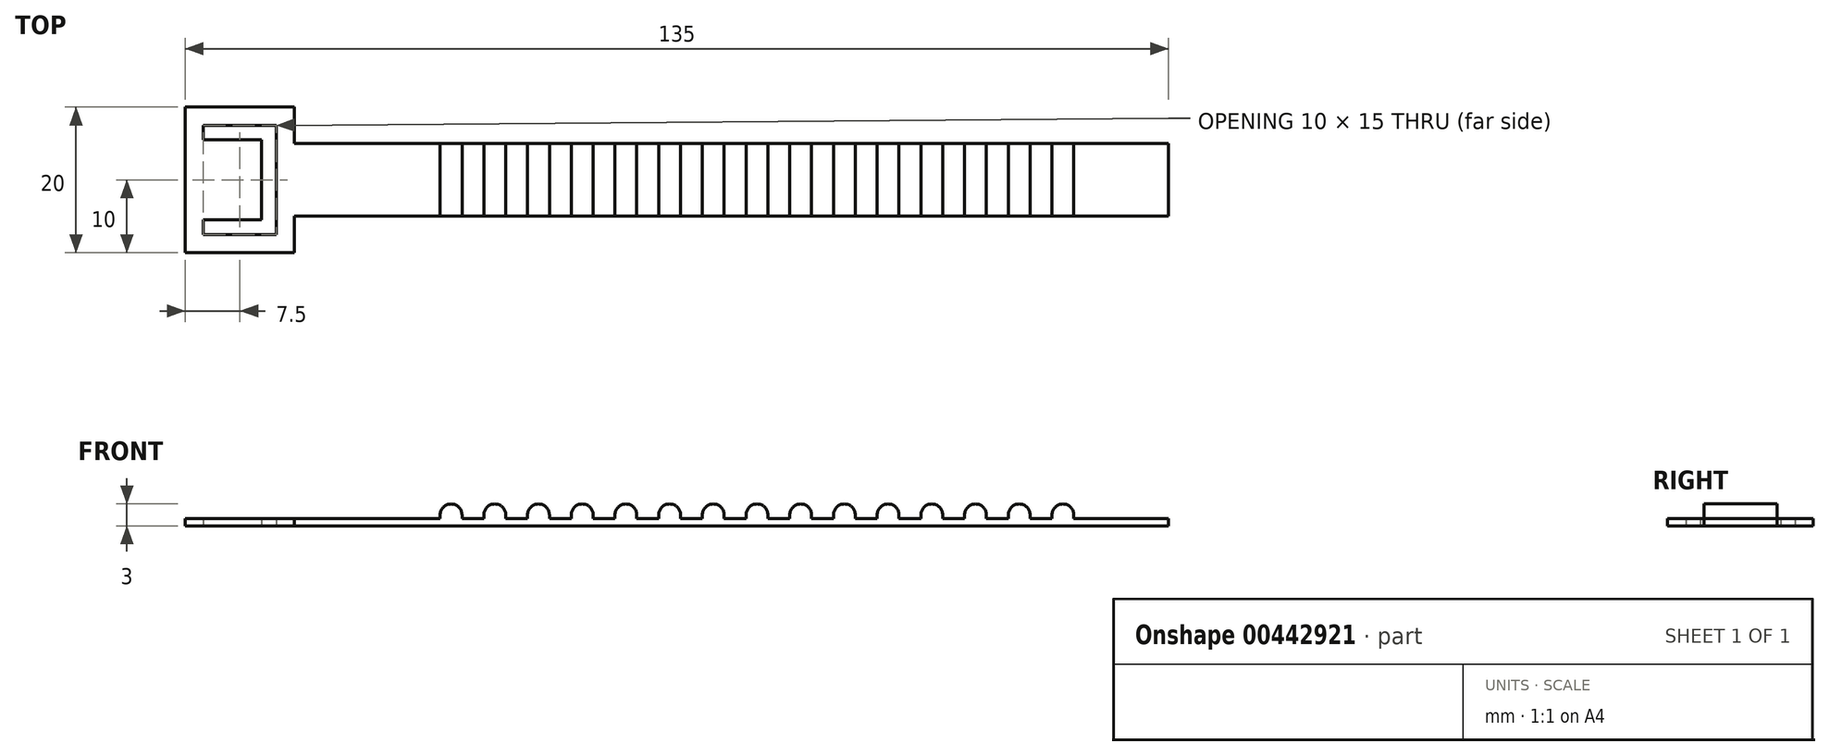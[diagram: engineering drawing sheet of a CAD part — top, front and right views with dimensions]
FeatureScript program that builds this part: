
annotation { "Feature Type Name" : "Feature", "Feature Type Description" : "" }
export const myFeature = defineFeature(function(context is Context, id is Id, definition is map)
    precondition{}
    {
        {
            var Q0;
            Q0=qCreatedBy(makeId("Top.planeOp"),FACE);
            var sketch = newSketch(context, id + "F0", { "sketchPlane" : qUnion([Q0])});
            skLineSegment(sketch, "E0.bottom", {"start": v(-60, 5) * mm, "end": v(60, 5) * mm});
            skLineSegment(sketch, "E0.top", {"start": v(-60, -5) * mm, "end": v(60, -5) * mm});
            skLineSegment(sketch, "E0.left", {"start": v(-60, 5) * mm, "end": v(-60, -5) * mm});
            skLineSegment(sketch, "E0.right", {"start": v(60, 5) * mm, "end": v(60, -5) * mm});
            skPoint(sketch, "E0.middle", {"position": v(0, 0) * mm});
            skLineSegment(sketch, "E1.bottom", {"start": v(-75, 10) * mm, "end": v(-60, 10) * mm});
            skLineSegment(sketch, "E1.top", {"start": v(-75, -10) * mm, "end": v(-60, -10) * mm});
            skLineSegment(sketch, "E1.left", {"start": v(-75, 10) * mm, "end": v(-75, -10) * mm});
            skLineSegment(sketch, "E1.right", {"start": v(-60, 10) * mm, "end": v(-60, -10) * mm});
            skPoint(sketch, "E1.middle", {"position": v(-67.5, 0) * mm});
            skLineSegment(sketch, "E2", {"start": v(-72.5, 7.5) * mm, "end": v(-62.5, 7.5) * mm});
            skLineSegment(sketch, "E3", {"start": v(-62.5, 7.5) * mm, "end": v(-62.5, -7.5) * mm});
            skLineSegment(sketch, "E4", {"start": v(-62.5, -7.5) * mm, "end": v(-72.5, -7.5) * mm});
            skLineSegment(sketch, "E5", {"start": v(-72.5, -7.5) * mm, "end": v(-72.5, -5.5) * mm});
            skLineSegment(sketch, "E6", {"start": v(-72.5, -5.5) * mm, "end": v(-64.5, -5.5) * mm});
            skLineSegment(sketch, "E7", {"start": v(-64.5, -5.5) * mm, "end": v(-64.5, 5.5) * mm});
            skLineSegment(sketch, "E8", {"start": v(-64.5, 5.5) * mm, "end": v(-72.5, 5.5) * mm});
            skLineSegment(sketch, "E9", {"start": v(-72.5, 5.5) * mm, "end": v(-72.5, 7.5) * mm});
            skSolve(sketch);
        }
        {
            var Q0;
            Q0 = qSketchRegion(id + "F0", true);
            extrude(context, id + "F1", {"entities" : qUnion([Q0]), "depth" : 1 * mm});
        }
        {
            var Q0;
            Q0=qCreatedBy(makeId("Top.planeOp"),FACE);
            var sketch = newSketch(context, id + "F2", { "sketchPlane" : qUnion([Q0])});
            skLineSegment(sketch, "E10.bottom", {"start": v(-37, 5) * mm, "end": v(-40, 5) * mm});
            skLineSegment(sketch, "E10.top", {"start": v(-37, -5) * mm, "end": v(-40, -5) * mm});
            skLineSegment(sketch, "E10.left", {"start": v(-37, 5) * mm, "end": v(-37, -5) * mm});
            skLineSegment(sketch, "E10.right", {"start": v(-40, 5) * mm, "end": v(-40, -5) * mm});
            skPoint(sketch, "E10.middle", {"position": v(-38.5, 0) * mm});
            skLineSegment(sketch, "E11.1.0.0", {"start": v(-34, 5) * mm, "end": v(-34, -5) * mm});
            skLineSegment(sketch, "E11.1.0.1", {"start": v(-31, 5) * mm, "end": v(-31, -5) * mm});
            skLineSegment(sketch, "E11.1.0.2", {"start": v(-31, 5) * mm, "end": v(-34, 5) * mm});
            skLineSegment(sketch, "E11.1.0.3", {"start": v(-31, -5) * mm, "end": v(-34, -5) * mm});
            skLineSegment(sketch, "E11.2.0.0", {"start": v(-28, 5) * mm, "end": v(-28, -5) * mm});
            skLineSegment(sketch, "E11.2.0.1", {"start": v(-25, 5) * mm, "end": v(-25, -5) * mm});
            skLineSegment(sketch, "E11.2.0.2", {"start": v(-25, 5) * mm, "end": v(-28, 5) * mm});
            skLineSegment(sketch, "E11.2.0.3", {"start": v(-25, -5) * mm, "end": v(-28, -5) * mm});
            skLineSegment(sketch, "E11.3.0.0", {"start": v(-22, 5) * mm, "end": v(-22, -5) * mm});
            skLineSegment(sketch, "E11.3.0.1", {"start": v(-19, 5) * mm, "end": v(-19, -5) * mm});
            skLineSegment(sketch, "E11.3.0.2", {"start": v(-19, 5) * mm, "end": v(-22, 5) * mm});
            skLineSegment(sketch, "E11.3.0.3", {"start": v(-19, -5) * mm, "end": v(-22, -5) * mm});
            skLineSegment(sketch, "E11.4.0.0", {"start": v(-16, 5) * mm, "end": v(-16, -5) * mm});
            skLineSegment(sketch, "E11.4.0.1", {"start": v(-13, 5) * mm, "end": v(-13, -5) * mm});
            skLineSegment(sketch, "E11.4.0.2", {"start": v(-13, 5) * mm, "end": v(-16, 5) * mm});
            skLineSegment(sketch, "E11.4.0.3", {"start": v(-13, -5) * mm, "end": v(-16, -5) * mm});
            skLineSegment(sketch, "E11.5.0.0", {"start": v(-10, 5) * mm, "end": v(-10, -5) * mm});
            skLineSegment(sketch, "E11.5.0.1", {"start": v(-7, 5) * mm, "end": v(-7, -5) * mm});
            skLineSegment(sketch, "E11.5.0.2", {"start": v(-7, 5) * mm, "end": v(-10, 5) * mm});
            skLineSegment(sketch, "E11.5.0.3", {"start": v(-7, -5) * mm, "end": v(-10, -5) * mm});
            skLineSegment(sketch, "E11.6.0.0", {"start": v(-4, 5) * mm, "end": v(-4, -5) * mm});
            skLineSegment(sketch, "E11.6.0.1", {"start": v(-1, 5) * mm, "end": v(-1, -5) * mm});
            skLineSegment(sketch, "E11.6.0.2", {"start": v(-1, 5) * mm, "end": v(-4, 5) * mm});
            skLineSegment(sketch, "E11.6.0.3", {"start": v(-1, -5) * mm, "end": v(-4, -5) * mm});
            skLineSegment(sketch, "E11.7.0.0", {"start": v(2, 5) * mm, "end": v(2, -5) * mm});
            skLineSegment(sketch, "E11.7.0.1", {"start": v(5, 5) * mm, "end": v(5, -5) * mm});
            skLineSegment(sketch, "E11.7.0.2", {"start": v(5, 5) * mm, "end": v(2, 5) * mm});
            skLineSegment(sketch, "E11.7.0.3", {"start": v(5, -5) * mm, "end": v(2, -5) * mm});
            skLineSegment(sketch, "E11.8.0.0", {"start": v(8, 5) * mm, "end": v(8, -5) * mm});
            skLineSegment(sketch, "E11.8.0.1", {"start": v(11, 5) * mm, "end": v(11, -5) * mm});
            skLineSegment(sketch, "E11.8.0.2", {"start": v(11, 5) * mm, "end": v(8, 5) * mm});
            skLineSegment(sketch, "E11.8.0.3", {"start": v(11, -5) * mm, "end": v(8, -5) * mm});
            skLineSegment(sketch, "E11.9.0.0", {"start": v(14, 5) * mm, "end": v(14, -5) * mm});
            skLineSegment(sketch, "E11.9.0.1", {"start": v(17, 5) * mm, "end": v(17, -5) * mm});
            skLineSegment(sketch, "E11.9.0.2", {"start": v(17, 5) * mm, "end": v(14, 5) * mm});
            skLineSegment(sketch, "E11.9.0.3", {"start": v(17, -5) * mm, "end": v(14, -5) * mm});
            skLineSegment(sketch, "E11.10.0.0", {"start": v(20, 5) * mm, "end": v(20, -5) * mm});
            skLineSegment(sketch, "E11.10.0.1", {"start": v(23, 5) * mm, "end": v(23, -5) * mm});
            skLineSegment(sketch, "E11.10.0.2", {"start": v(23, 5) * mm, "end": v(20, 5) * mm});
            skLineSegment(sketch, "E11.10.0.3", {"start": v(23, -5) * mm, "end": v(20, -5) * mm});
            skLineSegment(sketch, "E11.11.0.0", {"start": v(26, 5) * mm, "end": v(26, -5) * mm});
            skLineSegment(sketch, "E11.11.0.1", {"start": v(29, 5) * mm, "end": v(29, -5) * mm});
            skLineSegment(sketch, "E11.11.0.2", {"start": v(29, 5) * mm, "end": v(26, 5) * mm});
            skLineSegment(sketch, "E11.11.0.3", {"start": v(29, -5) * mm, "end": v(26, -5) * mm});
            skLineSegment(sketch, "E11.12.0.0", {"start": v(32, 5) * mm, "end": v(32, -5) * mm});
            skLineSegment(sketch, "E11.12.0.1", {"start": v(35, 5) * mm, "end": v(35, -5) * mm});
            skLineSegment(sketch, "E11.12.0.2", {"start": v(35, 5) * mm, "end": v(32, 5) * mm});
            skLineSegment(sketch, "E11.12.0.3", {"start": v(35, -5) * mm, "end": v(32, -5) * mm});
            skLineSegment(sketch, "E11.13.0.0", {"start": v(38, 5) * mm, "end": v(38, -5) * mm});
            skLineSegment(sketch, "E11.13.0.1", {"start": v(41, 5) * mm, "end": v(41, -5) * mm});
            skLineSegment(sketch, "E11.13.0.2", {"start": v(41, 5) * mm, "end": v(38, 5) * mm});
            skLineSegment(sketch, "E11.13.0.3", {"start": v(41, -5) * mm, "end": v(38, -5) * mm});
            skLineSegment(sketch, "E11.14.0.0", {"start": v(44, 5) * mm, "end": v(44, -5) * mm});
            skLineSegment(sketch, "E11.14.0.1", {"start": v(47, 5) * mm, "end": v(47, -5) * mm});
            skLineSegment(sketch, "E11.14.0.2", {"start": v(47, 5) * mm, "end": v(44, 5) * mm});
            skLineSegment(sketch, "E11.14.0.3", {"start": v(47, -5) * mm, "end": v(44, -5) * mm});
            skLineSegment(sketch, "E11.direction1", {"start": v(-40, -5) * mm, "end": v(-34, -5) * mm, "construction": true});
            skSolve(sketch);
        }
        {
            var Q0;
            Q0 = qSketchRegion(id + "F2", true);
            extrude(context, id + "F3", {"entities" : qUnion([Q0]), "operationType" : NewBodyOperationType.ADD, "depth" : 3 * mm});
        }
        {
            var Q0;
            Q0=makeQuery(id+"F3.opExtrude","CAP_EDGE",EDGE,{"disambiguationData":[OSD([sQuery(id+"F2.wireOp",EDGE,"E10.right")])],"isStart":false});
            fillet(context, id + "F4", {"entities" : qUnion([Q0]), "radius" : 1.5 * mm, "tangentPropagation" : true, "allowEdgeOverflow" : false});
        }
        {
            var Q0;
            Q0=makeQuery(id+"F3.opExtrude","CAP_EDGE",EDGE,{"disambiguationData":[OSD([sQuery(id+"F2.wireOp",EDGE,"E10.left")])],"isStart":false});
            fillet(context, id + "F5", {"entities" : qUnion([Q0]), "radius" : 1.5 * mm, "tangentPropagation" : true, "allowEdgeOverflow" : false});
        }
        {
            var Q0;
            Q0=makeQuery(id+"F3.opExtrude","CAP_EDGE",EDGE,{"disambiguationData":[OSD([sQuery(id+"F2.wireOp",EDGE,"E11.1.0.0")])],"isStart":false});
            var Q1;
            Q1=makeQuery(id+"F3.opExtrude","CAP_EDGE",EDGE,{"disambiguationData":[OSD([sQuery(id+"F2.wireOp",EDGE,"E11.1.0.1")])],"isStart":false});
            var Q2;
            Q2=makeQuery(id+"F3.opExtrude","CAP_EDGE",EDGE,{"disambiguationData":[OSD([sQuery(id+"F2.wireOp",EDGE,"E11.2.0.0")])],"isStart":false});
            var Q3;
            Q3=makeQuery(id+"F3.opExtrude","CAP_EDGE",EDGE,{"disambiguationData":[OSD([sQuery(id+"F2.wireOp",EDGE,"E11.2.0.1")])],"isStart":false});
            var Q4;
            Q4=makeQuery(id+"F3.opExtrude","CAP_EDGE",EDGE,{"disambiguationData":[OSD([sQuery(id+"F2.wireOp",EDGE,"E11.3.0.0")])],"isStart":false});
            var Q5;
            Q5=makeQuery(id+"F3.opExtrude","CAP_EDGE",EDGE,{"disambiguationData":[OSD([sQuery(id+"F2.wireOp",EDGE,"E11.3.0.1")])],"isStart":false});
            var Q6;
            Q6=makeQuery(id+"F3.opExtrude","CAP_EDGE",EDGE,{"disambiguationData":[OSD([sQuery(id+"F2.wireOp",EDGE,"E11.4.0.0")])],"isStart":false});
            var Q7;
            Q7=makeQuery(id+"F3.opExtrude","CAP_EDGE",EDGE,{"disambiguationData":[OSD([sQuery(id+"F2.wireOp",EDGE,"E11.4.0.1")])],"isStart":false});
            var Q8;
            Q8=makeQuery(id+"F3.opExtrude","CAP_EDGE",EDGE,{"disambiguationData":[OSD([sQuery(id+"F2.wireOp",EDGE,"E11.5.0.0")])],"isStart":false});
            var Q9;
            Q9=makeQuery(id+"F3.opExtrude","CAP_EDGE",EDGE,{"disambiguationData":[OSD([sQuery(id+"F2.wireOp",EDGE,"E11.5.0.1")])],"isStart":false});
            var Q10;
            Q10=makeQuery(id+"F3.opExtrude","CAP_EDGE",EDGE,{"disambiguationData":[OSD([sQuery(id+"F2.wireOp",EDGE,"E11.6.0.0")])],"isStart":false});
            var Q11;
            Q11=makeQuery(id+"F3.opExtrude","CAP_EDGE",EDGE,{"disambiguationData":[OSD([sQuery(id+"F2.wireOp",EDGE,"E11.6.0.1")])],"isStart":false});
            var Q12;
            Q12=makeQuery(id+"F3.opExtrude","CAP_EDGE",EDGE,{"disambiguationData":[OSD([sQuery(id+"F2.wireOp",EDGE,"E11.7.0.0")])],"isStart":false});
            var Q13;
            Q13=makeQuery(id+"F3.opExtrude","CAP_EDGE",EDGE,{"disambiguationData":[OSD([sQuery(id+"F2.wireOp",EDGE,"E11.7.0.1")])],"isStart":false});
            var Q14;
            Q14=makeQuery(id+"F3.opExtrude","CAP_EDGE",EDGE,{"disambiguationData":[OSD([sQuery(id+"F2.wireOp",EDGE,"E11.8.0.0")])],"isStart":false});
            var Q15;
            Q15=makeQuery(id+"F3.opExtrude","CAP_EDGE",EDGE,{"disambiguationData":[OSD([sQuery(id+"F2.wireOp",EDGE,"E11.8.0.1")])],"isStart":false});
            var Q16;
            Q16=makeQuery(id+"F3.opExtrude","CAP_EDGE",EDGE,{"disambiguationData":[OSD([sQuery(id+"F2.wireOp",EDGE,"E11.9.0.0")])],"isStart":false});
            var Q17;
            Q17=makeQuery(id+"F3.opExtrude","CAP_EDGE",EDGE,{"disambiguationData":[OSD([sQuery(id+"F2.wireOp",EDGE,"E11.9.0.1")])],"isStart":false});
            var Q18;
            Q18=makeQuery(id+"F3.opExtrude","CAP_EDGE",EDGE,{"disambiguationData":[OSD([sQuery(id+"F2.wireOp",EDGE,"E11.10.0.0")])],"isStart":false});
            var Q19;
            Q19=makeQuery(id+"F3.opExtrude","CAP_EDGE",EDGE,{"disambiguationData":[OSD([sQuery(id+"F2.wireOp",EDGE,"E11.10.0.1")])],"isStart":false});
            var Q20;
            Q20=makeQuery(id+"F3.opExtrude","CAP_EDGE",EDGE,{"disambiguationData":[OSD([sQuery(id+"F2.wireOp",EDGE,"E11.11.0.0")])],"isStart":false});
            var Q21;
            Q21=makeQuery(id+"F3.opExtrude","CAP_EDGE",EDGE,{"disambiguationData":[OSD([sQuery(id+"F2.wireOp",EDGE,"E11.11.0.1")])],"isStart":false});
            var Q22;
            Q22=makeQuery(id+"F3.opExtrude","CAP_EDGE",EDGE,{"disambiguationData":[OSD([sQuery(id+"F2.wireOp",EDGE,"E11.12.0.0")])],"isStart":false});
            var Q23;
            Q23=makeQuery(id+"F3.opExtrude","CAP_EDGE",EDGE,{"disambiguationData":[OSD([sQuery(id+"F2.wireOp",EDGE,"E11.12.0.1")])],"isStart":false});
            var Q24;
            Q24=makeQuery(id+"F3.opExtrude","CAP_EDGE",EDGE,{"disambiguationData":[OSD([sQuery(id+"F2.wireOp",EDGE,"E11.13.0.0")])],"isStart":false});
            var Q25;
            Q25=makeQuery(id+"F3.opExtrude","CAP_EDGE",EDGE,{"disambiguationData":[OSD([sQuery(id+"F2.wireOp",EDGE,"E11.13.0.1")])],"isStart":false});
            var Q26;
            Q26=makeQuery(id+"F3.opExtrude","CAP_EDGE",EDGE,{"disambiguationData":[OSD([sQuery(id+"F2.wireOp",EDGE,"E11.14.0.0")])],"isStart":false});
            var Q27;
            Q27=makeQuery(id+"F3.opExtrude","CAP_EDGE",EDGE,{"disambiguationData":[OSD([sQuery(id+"F2.wireOp",EDGE,"E11.14.0.1")])],"isStart":false});
            fillet(context, id + "F6", {"entities" : qUnion([Q0, Q1, Q2, Q3, Q4, Q5, Q6, Q7, Q8, Q9, Q10, Q11, Q12, Q13, Q14, Q15, Q16, Q17, Q18, Q19, Q20, Q21, Q22, Q23, Q24, Q25, Q26, Q27]), "radius" : 1.5 * mm, "tangentPropagation" : true, "allowEdgeOverflow" : false});
        }
    });
